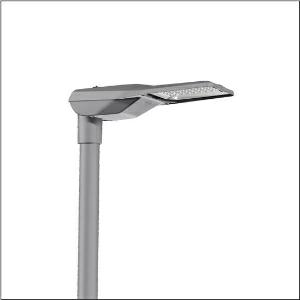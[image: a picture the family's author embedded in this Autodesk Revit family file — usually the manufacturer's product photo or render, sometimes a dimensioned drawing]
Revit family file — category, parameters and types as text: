
# Revit family: streetlight_sl_21_mini___st1_0a_5xe2d43s08jb_d214
name_source: partatom
category: Lighting Fixtures
units: mm (PartAtom-declared; Revit-internal decimal feet)

## family parameters
Cut with Voids When Loaded = No
Host = Face
Light Source = No
Part Type = Normal
Room Calculation Point = No
Round Connector Dimension = Use Diameter
Shared = No

## types (1)
- --- (1 x LED, 13390 lm, 87.3 W, 4000K)
    Apparent Load = 87 VA
    CIE Flux Codes = 40 73 97 100 100
    Color Rendering = 70
    Color Temperature = 4000K
    Default Elevation = 1800 mm
    Description = Streetlight SL 21 mini, mast luminaire, primary light control with lens, of PMMA, primary optical cover: cover, of toughened safety glass, transparent, light distribution: ST1.0a, light emission: direct distribution, primary light characteristic: asymmetric, installation type: side-entry, post-top, LED, High Power LED, rated luminous flux: 13.390lm, luminous efficacy: 153lm/W, light colour: 740, colour temperature: 4000K, control: overheat protection, constant luminous flux control, time-dependent luminous flux control, flexible luminous flux parameterisation, presetting dimming logarithmic, mains connection: 220..240V, AC, 50/60Hz, start of lifetime: 87W, end of service life: 90W, reduction: 40W, luminaire housing, of diecast aluminium, powder-coated, Siteco® metallic grey (DB 702S), corrosivity category C5 mid according to DIN EN ISO 12944, please order mast flange separately, inclination adjustable: 0°, 5°, 10°, 15°, sealing non-destructively replaceable, multi-level sealing system, length: 628mm, width: 235mm, height: 110mm, mast flange for spigot size: 42mm (side-entry): 5XC10008XM4, 60/48mm (side-entry/post-top): 5XC10108XM2, 76/60mm (side-entry/post-top): 5XC10108XM1, Smart Interface above, protection rating (complete): IP66, insulation class (complete): insulation class II (safety insulation), certification: CE, ENEC, ENEC+, VDE, impact resistance: IK09, permissible operating ambient temperature for outdoor applications: -40..+50°C, standard-compliant lighting for roads and squares, packaging unit: 1 piece

Light Distribution: ST1.0a
    Height = 110 mm
    Lamp = 1 x LED
    Lamp Light Flux = 13390 lm
    Lamp Power = 87.3 W
    Lamp count = 1
    Length = 625 mm
    Luminous efficacy = 153 lm/W
    Manufacturer = Siteco
    ModVariant = No
    Model = 5XE2D43S08JB
    Number of Poles = 1
    OnlyDefault = Yes
    Power Factor = 1
    Product Name = Streetlight SL 21 mini | ST1.0a
    Product group = mast luminaire | pylon top
    ProductGroupID = 6100
    Protection Class = Protection class II
    Protection Degree = IP 66
    RLX_Detail_Level = 1
    RLX_Emergency_Light_Flux = 0 lm
    RLX_Emergency_Type = 0
    RLX_Emergency_Type_DB = No
    RlxData = <blob elided: 92173 chars, md5=58ed443b>
    Socket = socket
    Standby Power = 0 W
    System Light Flux = 13390 lm
    System Power = 87 W
    Type Comments = factory setting: luminous flux: 100 % | dim-lin: 254 | 915 mA
    Type Image = l_1003515.jpg
    URL = http://relux.com
    VarID = @adj_103895
    Voltage = 0 V
    Weight = 0.00 kg
    Width = 234 mm

## geometry (parser evidence)
native form markers: Blend x4, Sweep x11
no freeform markers — native parametric forms only
